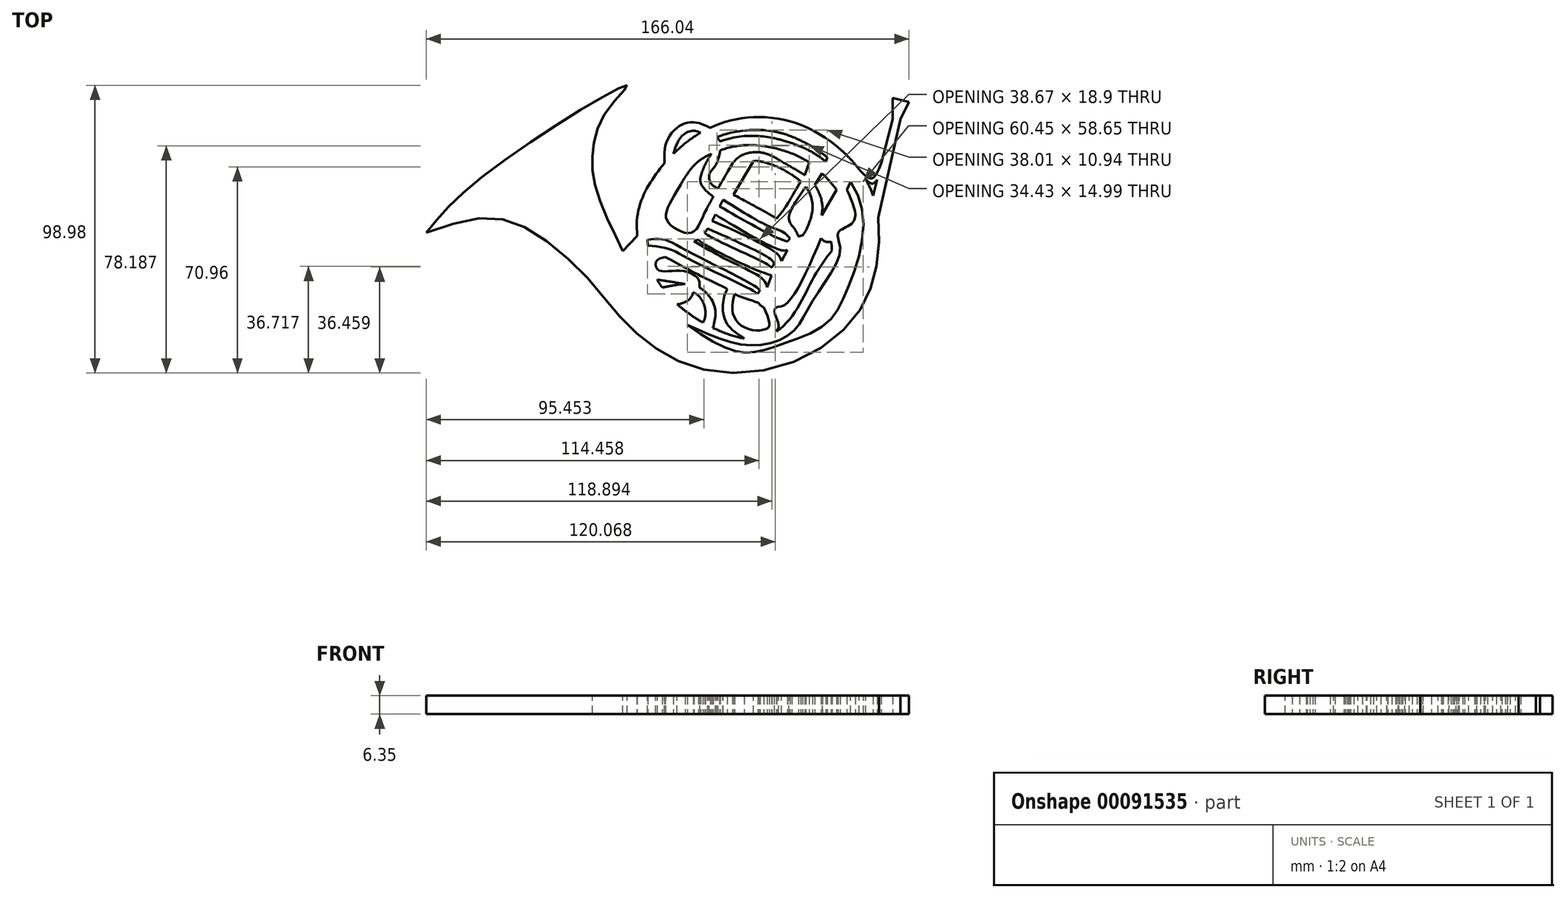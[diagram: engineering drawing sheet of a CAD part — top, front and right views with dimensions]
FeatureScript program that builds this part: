
annotation { "Feature Type Name" : "Feature", "Feature Type Description" : "" }
export const myFeature = defineFeature(function(context is Context, id is Id, definition is map)
    precondition{}
    {
        {
            var Q0;
            Q0=qCreatedBy(makeId("Top.planeOp"),FACE);
            var sketch = newSketch(context, id + "F0", { "sketchPlane" : qUnion([Q0])});
            skFitSpline(sketch, "E0", {"points": [v(-87.49, 0) * mm, v(-71.1, 16.93) * mm, v(-26.87, 46.7) * mm, v(-18.4, 50.52) * mm, v(-25.5, 41.78) * mm, v(-30.14, 28.4) * mm, v(-29.05, 14.75) * mm, v(-20.58, -4.92) * mm, v(-13.48, -17.75) * mm, v(2.35, -31.68) * mm, v(17.65, -40.41) * mm, v(26.11, -40.96) * mm, v(35.12, -38.23) * mm, v(49.6, -31.68) * mm, v(56.7, -21.03) * mm, v(62.7, 0) * mm, v(57.51, 18.84) * mm, v(37.58, 33.31) * mm, v(22.83, 35.23) * mm, v(9.18, 31.4) * mm, v(-5.02, 18.3) * mm, v(-11.3, 0) * mm, v(-6.38, -18.84) * mm, v(13, -33.59) * mm, v(28.57, -36.05) * mm, v(38.95, -27.85) * mm, v(45.77, -15.3) * mm, v(52.05, -6) * mm], "startDerivative": vector(290.63, 356.36) * mm, "endDerivative": vector(217.16, 289.85) * mm});
            skFitSpline(sketch, "E1", {"points": [v(-87.49, 0) * mm, v(-66.19, 5.18) * mm, v(-50.35, 0) * mm, v(-32.87, -14.75) * mm, v(-20.58, -29.22) * mm, v(-6.66, -40.96) * mm, v(13.82, -48.06) * mm, v(41.95, -43.15) * mm, v(60.8, -27.85) * mm, v(67.07, -12.56) * mm, v(67.9, 5.18) * mm, v(61.34, 21.85) * mm, v(39.76, 37.68) * mm, v(15.73, 38.23) * mm, v(0, 29.5) * mm, v(-10.48, 17.2) * mm, v(-15.12, 2.46) * mm, v(-8.74, -22.79) * mm], "startDerivative": vector(364.96, 127.59) * mm, "endDerivative": vector(145.17, -405.05) * mm});
            skLineSegment(sketch, "E2", {"start": v(67.9, 5.18) * mm, "end": v(75.52, 39.04) * mm});
            skLineSegment(sketch, "E3", {"start": v(75.52, 39.04) * mm, "end": v(78.55, 45.02) * mm});
            skLineSegment(sketch, "E4", {"start": v(78.55, 45.02) * mm, "end": v(72.88, 46.4) * mm});
            skLineSegment(sketch, "E5", {"start": v(72.88, 46.4) * mm, "end": v(72.88, 39.04) * mm});
            skLineSegment(sketch, "E6", {"start": v(72.88, 39.04) * mm, "end": v(68.92, 23.86) * mm});
            skLineSegment(sketch, "E7", {"start": v(68.92, 23.86) * mm, "end": v(66.2, 12.7) * mm});
            skFitSpline(sketch, "E8", {"points": [v(61.34, 21.85) * mm, v(65.67, 18.7) * mm, v(68.92, 23.86) * mm], "startDerivative": vector(9.6, -10.47) * mm, "endDerivative": vector(5.61, 14.24) * mm});
            skPoint(sketch, "E9.0.internal.snap0", {"position": v(67.56, 18.28) * mm});
            skFitSpline(sketch, "E9", {"points": [v(63.68, 18.28) * mm, v(66, 16.9) * mm, v(67.56, 18.28) * mm], "startDerivative": vector(4.63, -4.04) * mm, "endDerivative": vector(3.1, 4.22) * mm});
            skFitSpline(sketch, "E10", {"points": [v(2.35, -31.68) * mm, v(23.74, -38.75) * mm, v(38.3, -34.24) * mm, v(45.76, -22.79) * mm, v(54.93, -6.02) * mm, v(54.11, 0) * mm, v(59.1, 3.44) * mm, v(59.44, 9.28) * mm, v(52.34, 21.95) * mm, v(42.7, 29) * mm, v(33.1, 32.29) * mm, v(26.11, 33.31) * mm, v(17.73, 32.63) * mm, v(7.5, 28.86) * mm, v(1.12, 24.23) * mm, v(-5.06, 14.77) * mm, v(-8.05, 7.43) * mm, v(-6.38, 2.31) * mm, v(-2.07, -0.78) * mm, v(4.6, -2.9) * mm, v(11.35, 5.11) * mm, v(20.82, 21.91) * mm, v(26.8, 24.62) * mm, v(43.02, 15.73) * mm, v(44.57, 4.44) * mm, v(41.91, -0.99) * mm, v(41.91, -0.88) * mm], "startDerivative": vector(367.17, -171.12) * mm, "endDerivative": vector(6.43, 38.3) * mm});
            skFitSpline(sketch, "E11", {"points": [v(52.05, 3.13) * mm, v(56.52, 6.55) * mm, v(55.43, 11.87) * mm, v(48.6, 20.47) * mm, v(39.46, 26.75) * mm, v(24.44, 30.17) * mm, v(13.65, 28.4) * mm, v(5.05, 23.61) * mm, v(-1.37, 14.2) * mm, v(-5.06, 6) * mm, v(-2.87, 2.18) * mm, v(3.68, 0) * mm, v(8.05, 6.4) * mm, v(15.15, 19.24) * mm, v(19.52, 25.66) * mm, v(24.85, 27.7) * mm, v(30.3, 26.89) * mm, v(36.04, 23.75) * mm, v(42.73, 19.79) * mm, v(46.15, 16.38) * mm, v(48.74, 8.46) * mm, v(44.57, -3.1) * mm], "startDerivative": vector(147.24, 75.4) * mm, "endDerivative": vector(-110.63, -190.52) * mm});
            skFitSpline(sketch, "E12", {"points": [v(52.05, -6) * mm, v(51.74, -3.1) * mm], "startDerivative": vector(-0.95, 3.95) * mm, "endDerivative": vector(-0.95, 3.95) * mm});
            skCircle(sketch, "E13", {"center": v(50.9, 0) * mm, "radius": 3.22 * mm});
            skFitSpline(sketch, "E14", {"points": [v(50.15, 3.13) * mm, v(55.43, 11.87) * mm], "startDerivative": vector(5.28, 8.74) * mm, "endDerivative": vector(5.28, 8.74) * mm});
            skFitSpline(sketch, "E15", {"points": [v(57.1, 14.8) * mm, v(58.46, 17.5) * mm], "startDerivative": vector(1.35, 2.71) * mm, "endDerivative": vector(1.35, 2.71) * mm});
            skFitSpline(sketch, "E16", {"points": [v(48.48, 6.05) * mm, v(53.67, 14.8) * mm], "startDerivative": vector(5.2, 8.75) * mm, "endDerivative": vector(5.2, 8.75) * mm});
            skFitSpline(sketch, "E17", {"points": [v(48.3, -1.91) * mm, v(35.63, -24.88) * mm, v(32.54, -25.9) * mm, v(32.54, -28.23) * mm, v(33.7, -31.97) * mm, v(32.9, -34) * mm], "startDerivative": vector(-30.94, -72.33) * mm, "endDerivative": vector(-9.75, -14.88) * mm});
            skFitSpline(sketch, "E18", {"points": [v(21.9, -36.34) * mm, v(15.6, -30.72) * mm, v(14.7, -23.16) * mm, v(16.06, -19.42) * mm], "startDerivative": vector(-19.86, 12.56) * mm, "endDerivative": vector(6.23, 12.5) * mm});
            skCircle(sketch, "E19", {"center": v(39.84, -4.57) * mm, "radius": 3.4 * mm});
            skFitSpline(sketch, "E20", {"points": [v(41.91, -0.88) * mm, v(40.51, -1.23) * mm, v(40.5, -1.23) * mm], "startDerivative": vector(-2.18, -0.6) * mm, "endDerivative": vector(-0.11, 0.06) * mm});
            skFitSpline(sketch, "E21", {"points": [v(44.57, -3.1) * mm, v(43.49, -4.84) * mm], "startDerivative": vector(-1.08, -1.74) * mm, "endDerivative": vector(-1.08, -1.74) * mm});
            skCircle(sketch, "E22", {"center": v(34.74, -13.4) * mm, "radius": 3.67 * mm});
            skCircle(sketch, "E23", {"center": v(29.9, -22.34) * mm, "radius": 3.6 * mm});
            skFitSpline(sketch, "E24", {"points": [v(40.73, -7.85) * mm, v(38.23, -12.28) * mm], "startDerivative": vector(-2.5, -4.42) * mm, "endDerivative": vector(-2.5, -4.42) * mm});
            skFitSpline(sketch, "E25", {"points": [v(35.27, -17.04) * mm, v(33.42, -21.5) * mm], "startDerivative": vector(-1.85, -4.45) * mm, "endDerivative": vector(-1.85, -4.45) * mm});
            skFitSpline(sketch, "E26", {"points": [v(31.3, -14.7) * mm, v(29.73, -18.74) * mm], "startDerivative": vector(-1.58, -4.03) * mm, "endDerivative": vector(-1.58, -4.03) * mm});
            skFitSpline(sketch, "E27", {"points": [v(36.74, -5.97) * mm, v(34.64, -9.74) * mm], "startDerivative": vector(-2.1, -3.76) * mm, "endDerivative": vector(-2.1, -3.76) * mm});
            skFitSpline(sketch, "E28", {"points": [v(28.58, -25.69) * mm, v(30.46, -32) * mm, v(28.18, -33.46) * mm, v(21.98, -32.64) * mm, v(17.97, -27.8) * mm, v(18.52, -21.06) * mm], "startDerivative": vector(15.64, -34.27) * mm, "endDerivative": vector(7.37, 31.63) * mm});
            skFitSpline(sketch, "E29", {"points": [v(58.46, 17.5) * mm, v(58.46, 21.85) * mm, v(57.14, 26.64) * mm], "startDerivative": vector(0.63, 8.92) * mm, "endDerivative": vector(-3.27, 9.31) * mm});
            skFitSpline(sketch, "E30", {"points": [v(54.87, 28.75) * mm, v(49.69, 30.33) * mm, v(45.25, 29.53) * mm], "startDerivative": vector(-10.04, 4.33) * mm, "endDerivative": vector(-9.17, -2.87) * mm});
            skFitSpline(sketch, "E31", {"points": [v(56.38, 20.26) * mm, v(55.66, 24.02) * mm, v(53.13, 26.54) * mm, v(48.81, 27.17) * mm, v(48.74, 27.22) * mm], "startDerivative": vector(-1.3, 12.56) * mm, "endDerivative": vector(-0.64, 1.2) * mm});
            skFitSpline(sketch, "E32", {"points": [v(46.63, 26.87) * mm, v(44.18, 24.15) * mm], "startDerivative": vector(-2.45, -2.73) * mm, "endDerivative": vector(-2.45, -2.73) * mm});
            skFitSpline(sketch, "E33", {"points": [v(42.7, 29) * mm, v(41.22, 25.92) * mm], "startDerivative": vector(-1.5, -3.1) * mm, "endDerivative": vector(-1.5, -3.1) * mm});
            skFitSpline(sketch, "E34", {"points": [v(44.18, 24.15) * mm, v(42.73, 19.79) * mm], "startDerivative": vector(-1.45, -4.36) * mm, "endDerivative": vector(-1.45, -4.36) * mm});
            skFitSpline(sketch, "E35", {"points": [v(41.08, 25.97) * mm, v(39.2, 21.95) * mm], "startDerivative": vector(-1.9, -4.06) * mm, "endDerivative": vector(-1.9, -4.06) * mm});
            skFitSpline(sketch, "E36", {"points": [v(41.23, 17.63) * mm, v(35.56, 8.17) * mm, v(33.61, 5.65) * mm, v(33.04, 4.84) * mm], "startDerivative": vector(-11.34, -19.98) * mm, "endDerivative": vector(-3.05, -4.52) * mm});
            skFitSpline(sketch, "E37", {"points": [v(38.14, 20) * mm, v(32.92, 9.55) * mm, v(30.17, 6.57) * mm], "startDerivative": vector(-8.55, -19.3) * mm, "endDerivative": vector(-7.27, -6.46) * mm});
            skFitSpline(sketch, "E38", {"points": [v(40.51, -1.23) * mm, v(38.2, 2.43) * mm, v(33.04, 4.84) * mm], "startDerivative": vector(-3.86, 8.65) * mm, "endDerivative": vector(-10.93, 3.62) * mm});
            skFitSpline(sketch, "E39", {"points": [v(33.04, 4.84) * mm, v(30.17, 6.57) * mm, v(16.07, 14.2) * mm], "startDerivative": vector(-7.36, 4.6) * mm, "endDerivative": vector(-24.44, 13.03) * mm});
            skFitSpline(sketch, "E40", {"points": [v(37.59, -2.02) * mm, v(35.56, 0) * mm, v(29.94, 2.43) * mm, v(14.59, 11.37) * mm], "startDerivative": vector(-8.53, 10.77) * mm, "endDerivative": vector(-33.44, 21.12) * mm});
            skFitSpline(sketch, "E41", {"points": [v(36.82, -3.01) * mm, v(32.92, -1.59) * mm, v(13.4, 9.05) * mm], "startDerivative": vector(-10.64, 3.15) * mm, "endDerivative": vector(-33.22, 18.89) * mm});
            skFitSpline(sketch, "E42", {"points": [v(36.74, -5.97) * mm, v(34.42, -5.97) * mm, v(11.93, 6.21) * mm], "startDerivative": vector(-7.81, -1.84) * mm, "endDerivative": vector(-36.66, 21.96) * mm});
            skFitSpline(sketch, "E43", {"points": [v(34.64, -9.74) * mm, v(33.27, -7.33) * mm, v(10.83, 4.13) * mm], "startDerivative": vector(-2.45, 9) * mm, "endDerivative": vector(-39.05, 17.35) * mm});
            skFitSpline(sketch, "E44", {"points": [v(32.1, -10.87) * mm, v(31.55, -9.62) * mm, v(9.28, 1.43) * mm], "startDerivative": vector(-0.55, 5.89) * mm, "endDerivative": vector(-37.42, 16.5) * mm});
            skFitSpline(sketch, "E45", {"points": [v(31.3, -14.7) * mm, v(23.4, -11.69) * mm, v(6.98, -3.2) * mm, v(6.11, -2.24) * mm], "startDerivative": vector(-18.29, 6) * mm, "endDerivative": vector(-3.03, 5.61) * mm});
            skFitSpline(sketch, "E46", {"points": [v(31.4, -11.9) * mm, v(26.95, -9.4) * mm, v(9.73, -1.13) * mm, v(8.31, 0) * mm], "startDerivative": vector(-10.89, 7.03) * mm, "endDerivative": vector(-4.6, 5.27) * mm});
            skFitSpline(sketch, "E47", {"points": [v(29.73, -18.74) * mm, v(28.22, -15.94) * mm, v(17.3, -9.97) * mm, v(4.6, -2.9) * mm], "startDerivative": vector(-4.11, 14.17) * mm, "endDerivative": vector(-29.11, 17.22) * mm});
            skFitSpline(sketch, "E48", {"points": [v(-4.5, 0.65) * mm, v(-8.98, 1.05) * mm, v(-11.3, 0) * mm], "startDerivative": vector(-8.55, 1.63) * mm, "endDerivative": vector(-4.87, -3.14) * mm});
            skFitSpline(sketch, "E49", {"points": [v(27.3, -19.85) * mm, v(24.54, -17.77) * mm, v(1.7, -5.95) * mm, v(-6, -2.28) * mm, v(-11.37, -2.39) * mm], "startDerivative": vector(-11.32, 10.9) * mm, "endDerivative": vector(-29.01, -3.42) * mm});
            skFitSpline(sketch, "E50", {"points": [v(26.56, -21.02) * mm, v(22.7, -18.8) * mm, v(3.3, -9.28) * mm, v(-4.28, -5.49) * mm, v(-11.3, -4.48) * mm], "startDerivative": vector(-16.36, 10.4) * mm, "endDerivative": vector(-34.16, 2.57) * mm});
            skFitSpline(sketch, "E51", {"points": [v(26.75, -24.08) * mm, v(18.52, -21.06) * mm, v(16.06, -19.42) * mm, v(4.9, -13.87) * mm, v(-5.3, -8.36) * mm, v(-9.33, -7.33) * mm, v(-10.86, -8.02) * mm], "startDerivative": vector(-49.66, 15.98) * mm, "endDerivative": vector(-15.58, -10.59) * mm});
            skFitSpline(sketch, "E52", {"points": [v(-14.91, -1.1) * mm, v(-19.95, -6.28) * mm], "startDerivative": vector(-5.06, -5.2) * mm, "endDerivative": vector(-5.06, -5.2) * mm});
            skFitSpline(sketch, "E53", {"points": [v(-14.28, -4.94) * mm, v(-18.37, -9.64) * mm], "startDerivative": vector(-4.12, -4.7) * mm, "endDerivative": vector(-4.12, -4.7) * mm});
            skFitSpline(sketch, "E54", {"points": [v(-13.94, -7.04) * mm, v(-15.68, -9.07) * mm, v(-17.01, -12.33) * mm], "startDerivative": vector(-4.03, -3.92) * mm, "endDerivative": vector(-1.92, -6.48) * mm});
            skFitSpline(sketch, "E55", {"points": [v(-13.36, -9.93) * mm, v(-14.52, -12.68) * mm, v(-14.18, -16.85) * mm], "startDerivative": vector(-3.27, -5.61) * mm, "endDerivative": vector(1.6, -8.07) * mm});
            skFitSpline(sketch, "E56", {"points": [v(-13.48, -17.75) * mm, v(-10.1, -18.98) * mm, v(-6.38, -18.84) * mm, v(0, -17.75) * mm, v(6.46, -18.84) * mm, v(11.66, -25.41) * mm, v(11.12, -32.71) * mm], "startDerivative": vector(25.95, -11.74) * mm, "endDerivative": vector(-9.74, -39.1) * mm});
            skFitSpline(sketch, "E57", {"points": [v(-8.74, -22.79) * mm, v(-4.77, -20.93) * mm], "startDerivative": vector(3.98, 1.87) * mm, "endDerivative": vector(3.98, 1.87) * mm});
            skFitSpline(sketch, "E58", {"points": [v(-4.54, -21.07) * mm, v(1.4, -19.77) * mm, v(6.89, -22.52) * mm, v(8.48, -28.45) * mm, v(7.68, -30.9) * mm], "startDerivative": vector(21.36, 7.7) * mm, "endDerivative": vector(-5.85, -11.57) * mm});
            skFitSpline(sketch, "E59", {"points": [v(-5.3, -8.36) * mm, v(-8.3, -9.64) * mm, v(-8.16, -12.4) * mm, v(-5.3, -13.26) * mm, v(1.4, -13.26) * mm, v(6.17, -16) * mm, v(6.46, -18.84) * mm], "startDerivative": vector(-24.15, -4.47) * mm, "endDerivative": vector(-2.43, -20.35) * mm});
            skFitSpline(sketch, "E60", {"points": [v(-8.03, -16.17) * mm, v(-3.38, -16.88) * mm, v(1.59, -17.67) * mm], "startDerivative": vector(9.37, -1.44) * mm, "endDerivative": vector(9.86, -1.53) * mm});
            skFitSpline(sketch, "E61", {"points": [v(4.35, -20.5) * mm, v(2.55, -23.24) * mm, v(-1.2, -24.59) * mm, v(-1.6, -24.23) * mm], "startDerivative": vector(-2.87, -7.37) * mm, "endDerivative": vector(-1.4, 2.9) * mm});
            skFitSpline(sketch, "E62", {"points": [v(6.89, -22.52) * mm, v(4.86, -25.41) * mm, v(1.92, -27.14) * mm], "startDerivative": vector(-3.53, -6.3) * mm, "endDerivative": vector(-6.4, -2.9) * mm});
            skFitSpline(sketch, "E63", {"points": [v(9, 8.32) * mm, v(-1.37, 14.2) * mm], "startDerivative": vector(-10.6, 6) * mm, "endDerivative": vector(-10.6, 6) * mm});
            skFitSpline(sketch, "E64", {"points": [v(10.36, 11.33) * mm, v(0, 16.58) * mm], "startDerivative": vector(-10.36, 5.25) * mm, "endDerivative": vector(-10.36, 5.25) * mm});
            skFitSpline(sketch, "E65", {"points": [v(-3.02, 18.3) * mm, v(-3.98, 19.78) * mm, v(-3.78, 20.04) * mm], "startDerivative": vector(-2.03, 2.53) * mm, "endDerivative": vector(0.95, 0.68) * mm});
            skFitSpline(sketch, "E66", {"points": [v(-1.27, 21.08) * mm, v(-1.87, 22.4) * mm], "startDerivative": vector(-0.6, 1.32) * mm, "endDerivative": vector(-0.6, 1.32) * mm});
            skFitSpline(sketch, "E67", {"points": [v(-5.56, 23.93) * mm, v(-4.83, 31.31) * mm, v(0, 37) * mm, v(5.07, 37.97) * mm, v(10.13, 36.14) * mm], "startDerivative": vector(-1.16, 27.97) * mm, "endDerivative": vector(21.74, -10.39) * mm});
            skFitSpline(sketch, "E68", {"points": [v(-2.56, 27.1) * mm, v(0, 32.77) * mm, v(3.61, 35.05) * mm, v(6.87, 34.44) * mm], "startDerivative": vector(5.22, 16.01) * mm, "endDerivative": vector(11.25, -4.13) * mm});
            skFitSpline(sketch, "E69", {"points": [v(12.4, 32.9) * mm, v(13.54, 31.42) * mm], "startDerivative": vector(1.14, -1.49) * mm, "endDerivative": vector(1.14, -1.49) * mm});
            skFitSpline(sketch, "E70", {"points": [v(13.65, 28.4) * mm, v(11.9, 23.03) * mm, v(9.95, 20.43) * mm, v(10.27, 17.19) * mm, v(12.82, 15.18) * mm], "startDerivative": vector(-4.38, -19.9) * mm, "endDerivative": vector(13.3, -7.12) * mm});
            skFitSpline(sketch, "E71", {"points": [v(10.6, 27.2) * mm, v(8.19, 23) * mm, v(6.96, 19.58) * mm, v(7.37, 16.16) * mm, v(11.24, 12.44) * mm, v(11.28, 12.5) * mm], "startDerivative": vector(-10.3, -16.62) * mm, "endDerivative": vector(0.07, 2.77) * mm});
            skFitSpline(sketch, "E72", {"points": [v(9.18, 31.4) * mm, v(10.55, 30.27) * mm], "startDerivative": vector(1.37, -1.15) * mm, "endDerivative": vector(1.37, -1.15) * mm});
            skFitSpline(sketch, "E73", {"points": [v(13.53, 16.41) * mm, v(12.82, 18.69) * mm, v(11.9, 23.03) * mm], "startDerivative": vector(-1.96, 4.86) * mm, "endDerivative": vector(-1.5, 8.3) * mm});
            skFitSpline(sketch, "E74", {"points": [v(8.19, 23) * mm, v(4.43, 23) * mm], "startDerivative": vector(-3.75, 0) * mm, "endDerivative": vector(-3.75, 0) * mm});
            skFitSpline(sketch, "E75", {"points": [v(9.4, 25.88) * mm, v(7.34, 25.43) * mm], "startDerivative": vector(-2.05, -0.47) * mm, "endDerivative": vector(-2.05, -0.47) * mm});
            skFitSpline(sketch, "E76", {"points": [v(28.7, 24.26) * mm, v(21.66, 11.21) * mm], "startDerivative": vector(-7.05, -13.05) * mm, "endDerivative": vector(-7.05, -13.05) * mm});
            skFitSpline(sketch, "E77", {"points": [v(25.1, 24.8) * mm, v(18.14, 13.09) * mm], "startDerivative": vector(-6.95, -11.7) * mm, "endDerivative": vector(-6.95, -11.7) * mm});
            skFitSpline(sketch, "E78", {"points": [v(27.14, 29.98) * mm, v(24.85, 27.7) * mm], "startDerivative": vector(-2.3, -2.27) * mm, "endDerivative": vector(-2.3, -2.27) * mm});
            skFitSpline(sketch, "E79", {"points": [v(30.83, 29.02) * mm, v(30.3, 26.89) * mm], "startDerivative": vector(-0.52, -2.13) * mm, "endDerivative": vector(-0.52, -2.13) * mm});
            skFitSpline(sketch, "E80", {"points": [v(28.78, 33.26) * mm, v(31.1, 35.02) * mm], "startDerivative": vector(2.32, 1.76) * mm, "endDerivative": vector(2.32, 1.76) * mm});
            skFitSpline(sketch, "E81", {"points": [v(35.06, 34.21) * mm, v(33.1, 32.29) * mm], "startDerivative": vector(-1.96, -1.92) * mm, "endDerivative": vector(-1.96, -1.92) * mm});
            skFitSpline(sketch, "E82", {"points": [v(50.4, 25.96) * mm, v(49.88, 24.44) * mm], "startDerivative": vector(-0.53, -1.52) * mm, "endDerivative": vector(-0.53, -1.52) * mm});
            skFitSpline(sketch, "E83", {"points": [v(46.8, 26.84) * mm, v(48.81, 27.17) * mm], "startDerivative": vector(2, 0.33) * mm, "endDerivative": vector(2, 0.33) * mm});
            skFitSpline(sketch, "E84", {"points": [v(42.7, 29.3) * mm, v(45.25, 29.53) * mm], "startDerivative": vector(2.55, 0.24) * mm, "endDerivative": vector(2.55, 0.24) * mm});
            skFitSpline(sketch, "E85", {"points": [v(43.02, 15.73) * mm, v(37.24, 5.54) * mm, v(38.2, 2.43) * mm], "startDerivative": vector(-12.62, -17.71) * mm, "endDerivative": vector(4.78, -7.87) * mm});
            skFitSpline(sketch, "E86", {"points": [v(46.15, 16.38) * mm, v(48.6, 20.47) * mm], "startDerivative": vector(2.46, 4.1) * mm, "endDerivative": vector(2.46, 4.1) * mm});
            skFitSpline(sketch, "E87", {"points": [v(45.85, 22.6) * mm, v(43.96, 18.86) * mm], "startDerivative": vector(-1.88, -3.73) * mm, "endDerivative": vector(-1.88, -3.73) * mm});
            skFitSpline(sketch, "E88", {"points": [v(44.9, 12.1) * mm, v(40.66, 6.77) * mm, v(40.52, 4.31) * mm, v(43.8, 2.48) * mm], "startDerivative": vector(-12.2, -13.16) * mm, "endDerivative": vector(12.99, -4.85) * mm});
            skSolve(sketch);
        }
        {
            var Q0;
            {var subQ4=sQuery(id+"F0.wireOp",EDGE,"E50");Q0=makeQuery(id+"F0.imprint","IMPRINT",FACE,{"disambiguationData":[TD([[makeQuery(id+"F0.imprint","IMPRINT",EDGE,{"derivedFrom":subQ4}),1.0]])]});}
            var Q1;
            {var subQ0=sQuery(id+"F0.wireOp",EDGE,"E48");Q1=makeQuery(id+"F0.imprint","IMPRINT",FACE,{"disambiguationData":[TD([[makeQuery(id+"F0.imprint","IMPRINT",EDGE,{"derivedFrom":subQ0}),-1.0]])]});}
            var Q2;
            {var subQ0=sQuery(id+"F0.wireOp",EDGE,"E66");Q2=makeQuery(id+"F0.imprint","IMPRINT",FACE,{"disambiguationData":[TD([[makeQuery(id+"F0.imprint","IMPRINT",EDGE,{"derivedFrom":subQ0}),-1.0]])]});}
            var Q3;
            {var subQ9=sQuery(id+"F0.wireOp",EDGE,"E40");Q3=makeQuery(id+"F0.imprint","IMPRINT",FACE,{"disambiguationData":[TD([[makeQuery(id+"F0.imprint","IMPRINT",EDGE,{"derivedFrom":subQ9}),-1.0]])]});}
            var Q4;
            {var subQ0=sQuery(id+"F0.wireOp",EDGE,"E45");Q4=makeQuery(id+"F0.imprint","IMPRINT",FACE,{"disambiguationData":[TD([[makeQuery(id+"F0.imprint","IMPRINT",EDGE,{"derivedFrom":subQ0}),-1.0]])]});}
            var Q5;
            {var subQ0=sQuery(id+"F0.wireOp",EDGE,"E12");Q5=makeQuery(id+"F0.imprint","IMPRINT",FACE,{"disambiguationData":[TD([[makeQuery(id+"F0.imprint","IMPRINT",EDGE,{"derivedFrom":subQ0}),-1.0]])]});}
            var Q6;
            {var subQ13=sQuery(id+"F0.wireOp",EDGE,"E30");Q6=makeQuery(id+"F0.imprint","IMPRINT",FACE,{"disambiguationData":[TD([[makeQuery(id+"F0.imprint","IMPRINT",EDGE,{"derivedFrom":subQ13}),-1.0]])]});}
            var Q7;
            {var subQ0=sQuery(id+"F0.wireOp",EDGE,"E43");Q7=makeQuery(id+"F0.imprint","IMPRINT",FACE,{"disambiguationData":[TD([[makeQuery(id+"F0.imprint","IMPRINT",EDGE,{"derivedFrom":subQ0}),1.0]])]});}
            var Q8;
            {var subQ0=sQuery(id+"F0.wireOp",EDGE,"E41");Q8=makeQuery(id+"F0.imprint","IMPRINT",FACE,{"disambiguationData":[TD([[makeQuery(id+"F0.imprint","IMPRINT",EDGE,{"derivedFrom":subQ0}),1.0]])]});}
            var Q9;
            {var subQ0=sQuery(id+"F0.wireOp",EDGE,"E47");Q9=makeQuery(id+"F0.imprint","IMPRINT",FACE,{"disambiguationData":[TD([[makeQuery(id+"F0.imprint","IMPRINT",EDGE,{"derivedFrom":subQ0}),1.0]])]});}
            var Q10;
            {var subQ0=sQuery(id+"F0.wireOp",EDGE,"E24");Q10=makeQuery(id+"F0.imprint","IMPRINT",FACE,{"disambiguationData":[TD([[makeQuery(id+"F0.imprint","IMPRINT",EDGE,{"derivedFrom":subQ0}),-1.0]])]});}
            var Q11;
            {var subQ0=sQuery(id+"F0.wireOp",EDGE,"E36");Q11=makeQuery(id+"F0.imprint","IMPRINT",FACE,{"disambiguationData":[TD([[makeQuery(id+"F0.imprint","IMPRINT",EDGE,{"derivedFrom":subQ0}),1.0]])]});}
            var Q12;
            {var subQ0=sQuery(id+"F0.wireOp",EDGE,"E39");var subQ1=sQuery(id+"F0.wireOp",EDGE,"E10");var subQ2=makeQuery(id+"F0.imprint","INTERSECT",VERTEX,{"derivedFrom":[subQ1,subQ0]});Q12=makeQuery(id+"F0.imprint","IMPRINT",FACE,{"disambiguationData":[TD([[makeQuery(id+"F0.imprint","IMPRINT",EDGE,{"disambiguationData":[TD([[subQ2,-1.0]])],"derivedFrom":subQ1}),-1.0]])]});}
            var Q13;
            {var subQ0=sQuery(id+"F0.wireOp",EDGE,"E59");Q13=makeQuery(id+"F0.imprint","IMPRINT",FACE,{"disambiguationData":[TD([[makeQuery(id+"F0.imprint","IMPRINT",EDGE,{"derivedFrom":subQ0}),-1.0]])]});}
            var Q14;
            {var subQ0=sQuery(id+"F0.wireOp",EDGE,"E67");Q14=makeQuery(id+"F0.imprint","IMPRINT",FACE,{"disambiguationData":[TD([[makeQuery(id+"F0.imprint","IMPRINT",EDGE,{"derivedFrom":subQ0}),-1.0]])]});}
            var Q15;
            {var subQ1=sQuery(id+"F0.wireOp",EDGE,"E0");var subQ3=sQuery(id+"F0.wireOp",EDGE,"E56");var subQ4=makeQuery(id+"F0.imprint","INTERSECT",VERTEX,{"disambiguationData":[OD(0.0)],"derivedFrom":[subQ1,subQ3]});Q15=makeQuery(id+"F0.imprint","IMPRINT",FACE,{"disambiguationData":[TD([[makeQuery(id+"F0.imprint","IMPRINT",EDGE,{"disambiguationData":[TD([[subQ4,-1.0]])],"derivedFrom":subQ3}),-1.0]])]});}
            var Q16;
            {var subQ0=sQuery(id+"F0.wireOp",EDGE,"E22");var subQ3=makeQuery(id+"F0.imprint","INTERSECT",VERTEX,{"derivedFrom":[subQ0,sQuery(id+"F0.wireOp",EDGE,"E44")]});Q16=makeQuery(id+"F0.imprint","IMPRINT",FACE,{"disambiguationData":[TD([[makeQuery(id+"F0.imprint","IMPRINT",EDGE,{"disambiguationData":[TD([[subQ3,-1.0]])],"derivedFrom":subQ0}),1.0]])]});}
            var Q17;
            {var subQ0=sQuery(id+"F0.wireOp",EDGE,"E23");var subQ3=makeQuery(id+"F0.imprint","INTERSECT",VERTEX,{"derivedFrom":[subQ0,sQuery(id+"F0.wireOp",EDGE,"E49")]});Q17=makeQuery(id+"F0.imprint","IMPRINT",FACE,{"disambiguationData":[TD([[makeQuery(id+"F0.imprint","IMPRINT",EDGE,{"disambiguationData":[TD([[subQ3,-1.0]])],"derivedFrom":subQ0}),1.0]])]});}
            var Q18;
            {var subQ0=sQuery(id+"F0.wireOp",EDGE,"E15");Q18=makeQuery(id+"F0.imprint","IMPRINT",FACE,{"disambiguationData":[TD([[makeQuery(id+"F0.imprint","IMPRINT",EDGE,{"derivedFrom":subQ0}),1.0]])]});}
            var Q19;
            {var subQ0=sQuery(id+"F0.wireOp",EDGE,"E13");var subQ3=sQuery(id+"F0.wireOp",EDGE,"E10");var subQ4=makeQuery(id+"F0.imprint","INTERSECT",VERTEX,{"disambiguationData":[OD(0.0)],"derivedFrom":[subQ3,subQ0]});Q19=makeQuery(id+"F0.imprint","IMPRINT",FACE,{"disambiguationData":[TD([[makeQuery(id+"F0.imprint","IMPRINT",EDGE,{"disambiguationData":[TD([[subQ4,-1.0]])],"derivedFrom":subQ3}),1.0]])]});}
            var Q20;
            {var subQ0=sQuery(id+"F0.wireOp",EDGE,"E61");var subQ1=sQuery(id+"F0.wireOp",EDGE,"E0");var subQ2=makeQuery(id+"F0.imprint","INTERSECT",VERTEX,{"disambiguationData":[OD(0.0)],"derivedFrom":[subQ1,subQ0]});Q20=makeQuery(id+"F0.imprint","IMPRINT",FACE,{"disambiguationData":[TD([[makeQuery(id+"F0.imprint","IMPRINT",EDGE,{"disambiguationData":[TD([[subQ2,-1.0]])],"derivedFrom":subQ1}),-1.0]])]});}
            var Q21;
            {var subQ0=sQuery(id+"F0.wireOp",EDGE,"E52");Q21=makeQuery(id+"F0.imprint","IMPRINT",FACE,{"disambiguationData":[TD([[makeQuery(id+"F0.imprint","IMPRINT",EDGE,{"derivedFrom":subQ0}),1.0]])]});}
            var Q22;
            {var subQ0=sQuery(id+"F0.wireOp",EDGE,"E31");var subQ1=sQuery(id+"F0.wireOp",EDGE,"E0");var subQ2=makeQuery(id+"F0.imprint","INTERSECT",VERTEX,{"disambiguationData":[OD(0.0)],"derivedFrom":[subQ1,subQ0]});Q22=makeQuery(id+"F0.imprint","IMPRINT",FACE,{"disambiguationData":[TD([[makeQuery(id+"F0.imprint","IMPRINT",EDGE,{"disambiguationData":[TD([[subQ2,-1.0]])],"derivedFrom":subQ1}),-1.0]])]});}
            var Q23;
            {var subQ0=sQuery(id+"F0.wireOp",EDGE,"E70");var subQ1=sQuery(id+"F0.wireOp",EDGE,"E11");var subQ2=makeQuery(id+"F0.imprint","INTERSECT",VERTEX,{"disambiguationData":[OD(0.0)],"derivedFrom":[subQ1,subQ0]});Q23=makeQuery(id+"F0.imprint","IMPRINT",FACE,{"disambiguationData":[TD([[makeQuery(id+"F0.imprint","IMPRINT",EDGE,{"disambiguationData":[TD([[subQ2,-1.0]])],"derivedFrom":subQ1}),1.0]])]});}
            var Q24;
            {var subQ0=sQuery(id+"F0.wireOp",EDGE,"E57");Q24=makeQuery(id+"F0.imprint","IMPRINT",FACE,{"disambiguationData":[TD([[makeQuery(id+"F0.imprint","IMPRINT",EDGE,{"derivedFrom":subQ0}),1.0]])]});}
            var Q25;
            {var subQ0=sQuery(id+"F0.wireOp",EDGE,"E19");var subQ5=sQuery(id+"F0.wireOp",EDGE,"E20");var subQ6=makeQuery(id+"F0.imprint","INTERSECT",VERTEX,{"derivedFrom":[subQ0,subQ5]});Q25=makeQuery(id+"F0.imprint","IMPRINT",FACE,{"disambiguationData":[TD([[makeQuery(id+"F0.imprint","IMPRINT",EDGE,{"disambiguationData":[TD([[subQ6,-1.0]])],"derivedFrom":subQ0}),1.0]])]});}
            var Q26;
            {var subQ0=sQuery(id+"F0.wireOp",EDGE,"E69");Q26=makeQuery(id+"F0.imprint","IMPRINT",FACE,{"disambiguationData":[TD([[makeQuery(id+"F0.imprint","IMPRINT",EDGE,{"derivedFrom":subQ0}),-1.0]])]});}
            var Q27;
            {var subQ0=sQuery(id+"F0.wireOp",EDGE,"E25");Q27=makeQuery(id+"F0.imprint","IMPRINT",FACE,{"disambiguationData":[TD([[makeQuery(id+"F0.imprint","IMPRINT",EDGE,{"derivedFrom":subQ0}),-1.0]])]});}
            var Q28;
            {var subQ0=sQuery(id+"F0.wireOp",EDGE,"E8");Q28=makeQuery(id+"F0.imprint","IMPRINT",FACE,{"disambiguationData":[TD([[makeQuery(id+"F0.imprint","IMPRINT",EDGE,{"derivedFrom":subQ0}),-1.0]])]});}
            var Q29;
            {var subQ6=sQuery(id+"F0.wireOp",EDGE,"E66");Q29=makeQuery(id+"F0.imprint","IMPRINT",FACE,{"disambiguationData":[TD([[makeQuery(id+"F0.imprint","IMPRINT",EDGE,{"derivedFrom":subQ6}),1.0]])]});}
            var Q30;
            {var subQ0=sQuery(id+"F0.wireOp",EDGE,"E13");var subQ1=sQuery(id+"F0.wireOp",EDGE,"E10");var subQ2=makeQuery(id+"F0.imprint","INTERSECT",VERTEX,{"disambiguationData":[OD(0.0)],"derivedFrom":[subQ1,subQ0]});Q30=makeQuery(id+"F0.imprint","IMPRINT",FACE,{"disambiguationData":[TD([[makeQuery(id+"F0.imprint","IMPRINT",EDGE,{"disambiguationData":[TD([[subQ2,-1.0]])],"derivedFrom":subQ1}),-1.0]])]});}
            var Q31;
            {var subQ0=sQuery(id+"F0.wireOp",EDGE,"E71");var subQ1=sQuery(id+"F0.wireOp",EDGE,"E11");var subQ2=makeQuery(id+"F0.imprint","INTERSECT",VERTEX,{"disambiguationData":[OD(1.0)],"derivedFrom":[subQ1,subQ0]});Q31=makeQuery(id+"F0.imprint","IMPRINT",FACE,{"disambiguationData":[TD([[makeQuery(id+"F0.imprint","IMPRINT",EDGE,{"disambiguationData":[TD([[subQ2,1.0]])],"derivedFrom":subQ1}),-1.0]])]});}
            var Q32;
            {var subQ3=sQuery(id+"F0.wireOp",EDGE,"E34");Q32=makeQuery(id+"F0.imprint","IMPRINT",FACE,{"disambiguationData":[TD([[makeQuery(id+"F0.imprint","IMPRINT",EDGE,{"derivedFrom":subQ3}),1.0]])]});}
            var Q33;
            {var subQ0=sQuery(id+"F0.wireOp",EDGE,"E65");var subQ1=sQuery(id+"F0.wireOp",EDGE,"E0");var subQ2=makeQuery(id+"F0.imprint","INTERSECT",VERTEX,{"disambiguationData":[OD(0.0)],"derivedFrom":[subQ1,subQ0]});Q33=makeQuery(id+"F0.imprint","IMPRINT",FACE,{"disambiguationData":[TD([[makeQuery(id+"F0.imprint","IMPRINT",EDGE,{"disambiguationData":[TD([[subQ2,-1.0]])],"derivedFrom":subQ1}),-1.0]])]});}
            var Q34;
            {var subQ0=sQuery(id+"F0.wireOp",EDGE,"E32");Q34=makeQuery(id+"F0.imprint","IMPRINT",FACE,{"disambiguationData":[TD([[makeQuery(id+"F0.imprint","IMPRINT",EDGE,{"derivedFrom":subQ0}),-1.0]])]});}
            var Q35;
            {var subQ0=sQuery(id+"F0.wireOp",EDGE,"E31");var subQ1=sQuery(id+"F0.wireOp",EDGE,"E0");var subQ2=makeQuery(id+"F0.imprint","INTERSECT",VERTEX,{"disambiguationData":[OD(1.0)],"derivedFrom":[subQ1,subQ0]});Q35=makeQuery(id+"F0.imprint","IMPRINT",FACE,{"disambiguationData":[TD([[makeQuery(id+"F0.imprint","IMPRINT",EDGE,{"disambiguationData":[TD([[subQ2,1.0]])],"derivedFrom":subQ1}),1.0]])]});}
            var Q36;
            {var subQ0=sQuery(id+"F0.wireOp",EDGE,"E20");var subQ1=sQuery(id+"F0.wireOp",EDGE,"E19");var subQ2=makeQuery(id+"F0.imprint","INTERSECT",VERTEX,{"derivedFrom":[subQ1,subQ0]});Q36=makeQuery(id+"F0.imprint","IMPRINT",FACE,{"disambiguationData":[TD([[makeQuery(id+"F0.imprint","IMPRINT",EDGE,{"disambiguationData":[TD([[subQ2,1.0]])],"derivedFrom":subQ1}),1.0]])]});}
            var Q37;
            {var subQ2=sQuery(id+"F0.wireOp",EDGE,"E29");Q37=makeQuery(id+"F0.imprint","IMPRINT",FACE,{"disambiguationData":[TD([[makeQuery(id+"F0.imprint","IMPRINT",EDGE,{"derivedFrom":subQ2}),-1.0]])]});}
            var Q38;
            {var subQ5=sQuery(id+"F0.wireOp",EDGE,"E14");Q38=makeQuery(id+"F0.imprint","IMPRINT",FACE,{"disambiguationData":[TD([[makeQuery(id+"F0.imprint","IMPRINT",EDGE,{"derivedFrom":subQ5}),1.0]])]});}
            var Q39;
            {var subQ0=sQuery(id+"F0.wireOp",EDGE,"E2");Q39=makeQuery(id+"F0.imprint","IMPRINT",FACE,{"disambiguationData":[TD([[makeQuery(id+"F0.imprint","IMPRINT",EDGE,{"derivedFrom":subQ0}),1.0]])]});}
            var Q40;
            {var subQ1=sQuery(id+"F0.wireOp",EDGE,"E0");var subQ8=makeQuery(id+"F0.imprint","INTERSECT",VERTEX,{"derivedFrom":[subQ1,sQuery(id+"F0.wireOp",EDGE,"E57")]});Q40=makeQuery(id+"F0.imprint","IMPRINT",FACE,{"disambiguationData":[TD([[makeQuery(id+"F0.imprint","IMPRINT",EDGE,{"disambiguationData":[TD([[subQ8,1.0]])],"derivedFrom":subQ1}),1.0]])]});}
            var Q41;
            {var subQ0=sQuery(id+"F0.wireOp",EDGE,"E53");Q41=makeQuery(id+"F0.imprint","IMPRINT",FACE,{"disambiguationData":[TD([[makeQuery(id+"F0.imprint","IMPRINT",EDGE,{"derivedFrom":subQ0}),1.0]])]});}
            var Q42;
            {var subQ0=sQuery(id+"F0.wireOp",EDGE,"E14");Q42=makeQuery(id+"F0.imprint","IMPRINT",FACE,{"disambiguationData":[TD([[makeQuery(id+"F0.imprint","IMPRINT",EDGE,{"derivedFrom":subQ0}),-1.0]])]});}
            var Q43;
            {var subQ4=sQuery(id+"F0.wireOp",EDGE,"E29");Q43=makeQuery(id+"F0.imprint","IMPRINT",FACE,{"disambiguationData":[TD([[makeQuery(id+"F0.imprint","IMPRINT",EDGE,{"derivedFrom":subQ4}),1.0]])]});}
            extrude(context, id + "F1", {"entities" : qUnion([Q0, Q1, Q2, Q3, Q4, Q5, Q6, Q7, Q8, Q9, Q10, Q11, Q12, Q13, Q14, Q15, Q16, Q17, Q18, Q19, Q20, Q21, Q22, Q23, Q24, Q25, Q26, Q27, Q28, Q29, Q30, Q31, Q32, Q33, Q34, Q35, Q36, Q37, Q38, Q39, Q40, Q41, Q42, Q43]), "depth" : 6.35 * mm});
        }
    });
